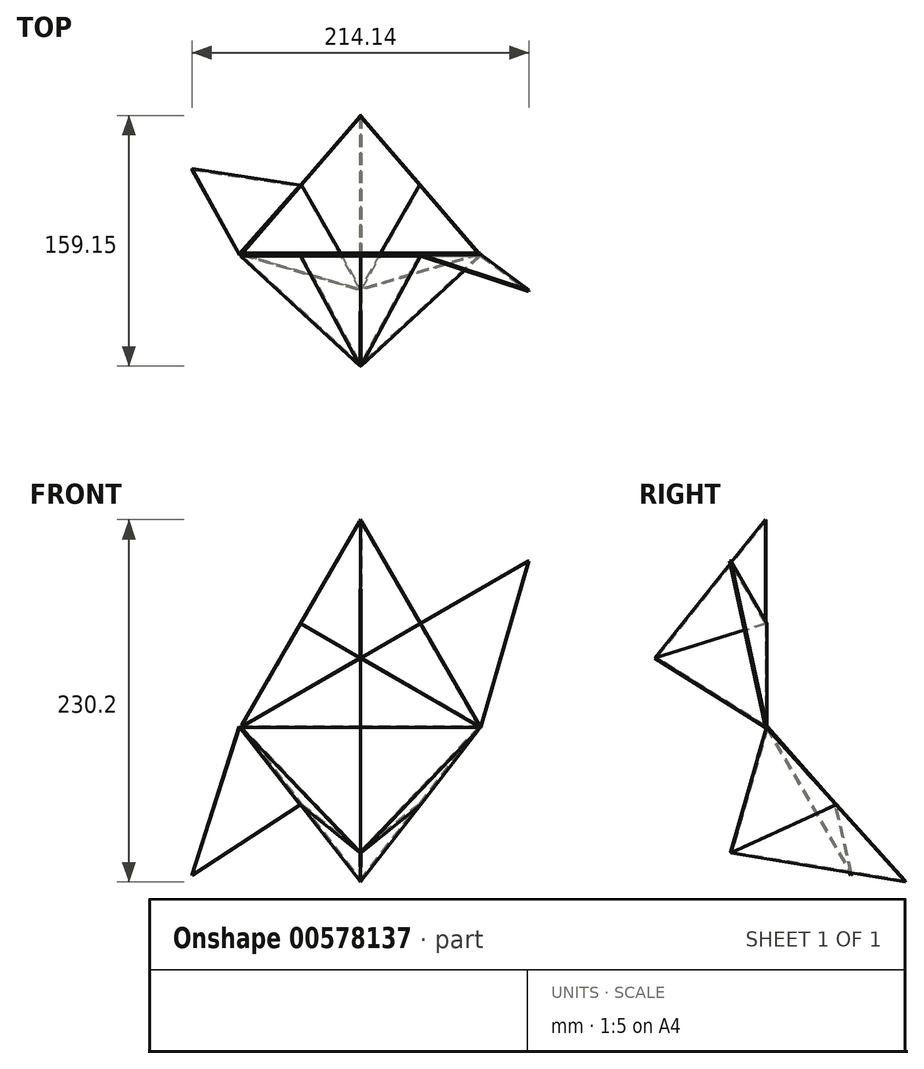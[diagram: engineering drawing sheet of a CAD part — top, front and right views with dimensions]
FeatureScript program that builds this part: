
annotation { "Feature Type Name" : "Feature", "Feature Type Description" : "" }
export const myFeature = defineFeature(function(context is Context, id is Id, definition is map)
    precondition{}
    {
        {
            var Q0;
            Q0=qCreatedBy(makeId("Front.planeOp"),FACE);
            var sketch = newSketch(context, id + "F0", { "sketchPlane" : qUnion([Q0])});
            skLineSegment(sketch, "E0", {"start": v(0, 0) * mm, "end": v(76.2, 0) * mm});
            skLineSegment(sketch, "E1", {"start": v(76.2, 0) * mm, "end": v(152.4, 0) * mm});
            skLineSegment(sketch, "E2", {"start": v(76.2, 0) * mm, "end": v(76.2, -82.55) * mm});
            skLineSegment(sketch, "E3", {"start": v(0, 0) * mm, "end": v(38.1, 66) * mm});
            skLineSegment(sketch, "E4", {"start": v(38.1, 66) * mm, "end": v(76.2, 131.98) * mm});
            skLineSegment(sketch, "E5", {"start": v(76.2, 131.98) * mm, "end": v(114.3, 66) * mm});
            skLineSegment(sketch, "E6", {"start": v(114.3, 66) * mm, "end": v(152.4, 0) * mm});
            skLineSegment(sketch, "E7", {"start": v(38.1, 66) * mm, "end": v(-33.4, 107.27) * mm});
            skLineSegment(sketch, "E8", {"start": v(114.3, 66) * mm, "end": v(185.8, 107.27) * mm});
            skLineSegment(sketch, "E9", {"start": v(0, 0) * mm, "end": v(76.2, -82.55) * mm});
            skLineSegment(sketch, "E10", {"start": v(152.4, 0) * mm, "end": v(76.2, -82.55) * mm});
            skLineSegment(sketch, "E11", {"start": v(76.2, 131.98) * mm, "end": v(185.8, 107.27) * mm});
            skLineSegment(sketch, "E12", {"start": v(152.4, 0) * mm, "end": v(185.8, 107.27) * mm});
            skLineSegment(sketch, "E13", {"start": v(76.2, 131.98) * mm, "end": v(-33.4, 107.27) * mm});
            skLineSegment(sketch, "E14", {"start": v(-33.4, 107.27) * mm, "end": v(0, 0) * mm});
            skSolve(sketch);
        }
        {
            var Q0;
            Q0=makeQuery(id+"F0.imprint","IMPRINT",FACE,{"disambiguationData":[TD([[makeQuery(id+"F0.imprint","IMPRINT",EDGE,{"derivedFrom":sQuery(id+"F0.wireOp",EDGE,"E4")}),1.0]])]});
            var Q1;
            Q1=makeQuery(id+"F0.imprint","IMPRINT",FACE,{"disambiguationData":[TD([[makeQuery(id+"F0.imprint","IMPRINT",EDGE,{"derivedFrom":sQuery(id+"F0.wireOp",EDGE,"E0")}),-1.0]])]});
            var Q2;
            Q2=makeQuery(id+"F0.imprint","IMPRINT",FACE,{"disambiguationData":[TD([[makeQuery(id+"F0.imprint","IMPRINT",EDGE,{"derivedFrom":sQuery(id+"F0.wireOp",EDGE,"E6")}),1.0]])]});
            extrude(context, id + "F1", {"entities" : qUnion([Q0, Q1, Q2]), "depth" : 1.02 * mm, "offsetDistance" : 25.4 * mm});
        }
        {
            var Q0;
            Q0=makeQuery(id+"F1.opExtrude","SWEPT_BODY",BODY,{"disambiguationData":[OSD([sQuery(id+"F0.wireOp",EDGE,"E3"),sQuery(id+"F0.wireOp",EDGE,"E4"),sQuery(id+"F0.wireOp",EDGE,"E13"),sQuery(id+"F0.wireOp",EDGE,"E14")])]});
            var Q1;
            Q1=makeQuery(id+"F1.opExtrude","CAP_EDGE",EDGE,{"disambiguationData":[OSD([sQuery(id+"F0.wireOp",EDGE,"E3"),sQuery(id+"F0.wireOp",EDGE,"E4")])],"isStart":true});
            transform(context, id + "F2", {"entities" : qUnion([Q0]), "transformType" : TransformType.ROTATION, "transformAxis" : qUnion([Q1]), "angle" : 122 * degree, "makeCopy" : false});
        }
        {
            var Q0;
            Q0=makeQuery(id+"F1.opExtrude","SWEPT_BODY",BODY,{"disambiguationData":[OSD([sQuery(id+"F0.wireOp",EDGE,"E0"),sQuery(id+"F0.wireOp",EDGE,"E1"),sQuery(id+"F0.wireOp",EDGE,"E9"),sQuery(id+"F0.wireOp",EDGE,"E10")])]});
            var Q1;
            Q1=makeQuery(id+"F1.opExtrude","CAP_EDGE",EDGE,{"disambiguationData":[OSD([sQuery(id+"F0.wireOp",EDGE,"E0"),sQuery(id+"F0.wireOp",EDGE,"E1")])],"isStart":true});
            transform(context, id + "F3", {"entities" : qUnion([Q0]), "transformType" : TransformType.ROTATION, "transformAxis" : qUnion([Q1]), "angle" : 122 * degree, "oppositeDirection" : true, "makeCopy" : false});
        }
        {
            var Q0;
            Q0=makeQuery(id+"F1.opExtrude","SWEPT_BODY",BODY,{"disambiguationData":[OSD([sQuery(id+"F0.wireOp",EDGE,"E5"),sQuery(id+"F0.wireOp",EDGE,"E6"),sQuery(id+"F0.wireOp",EDGE,"E11"),sQuery(id+"F0.wireOp",EDGE,"E12")])]});
            var Q1;
            Q1=makeQuery(id+"F1.opExtrude","CAP_EDGE",EDGE,{"disambiguationData":[OSD([sQuery(id+"F0.wireOp",EDGE,"E5"),sQuery(id+"F0.wireOp",EDGE,"E6")])],"isStart":true});
            transform(context, id + "F4", {"entities" : qUnion([Q0]), "transformType" : TransformType.ROTATION, "transformAxis" : qUnion([Q1]), "angle" : 122 * degree, "makeCopy" : false});
        }
        {
            var Q0;
            Q0=makeQuery(id+"F0.imprint","IMPRINT",FACE,{"disambiguationData":[TD([[makeQuery(id+"F0.imprint","IMPRINT",EDGE,{"derivedFrom":sQuery(id+"F0.wireOp",EDGE,"E6")}),1.0]])]});
            extrude(context, id + "F5", {"entities" : qUnion([Q0]), "oppositeDirection" : true, "depth" : 1.02 * mm, "offsetDistance" : 25.4 * mm});
        }
        {
            var Q0;
            Q0=makeQuery(id+"F1.opExtrude","SWEPT_BODY",BODY,{"disambiguationData":[OSD([sQuery(id+"F0.wireOp",EDGE,"E3"),sQuery(id+"F0.wireOp",EDGE,"E4"),sQuery(id+"F0.wireOp",EDGE,"E13"),sQuery(id+"F0.wireOp",EDGE,"E14")])]});
            var Q1;
            Q1=makeQuery(id+"F1.opExtrude","SWEPT_BODY",BODY,{"disambiguationData":[OSD([sQuery(id+"F0.wireOp",EDGE,"E5"),sQuery(id+"F0.wireOp",EDGE,"E6"),sQuery(id+"F0.wireOp",EDGE,"E11"),sQuery(id+"F0.wireOp",EDGE,"E12")])]});
            var Q2;
            Q2=makeQuery(id+"F1.opExtrude","SWEPT_BODY",BODY,{"disambiguationData":[OSD([sQuery(id+"F0.wireOp",EDGE,"E0"),sQuery(id+"F0.wireOp",EDGE,"E1"),sQuery(id+"F0.wireOp",EDGE,"E9"),sQuery(id+"F0.wireOp",EDGE,"E10")])]});
            var Q3;
            Q3=qCreatedBy(makeId("Top.planeOp"),FACE);
            mirror(context, id + "F6", {"entities" : qUnion([Q0, Q1, Q2]), "mirrorPlane" : qUnion([Q3])});
        }
        {
            var Q0;
            Q0=makeQuery(id+"F6.opPattern","COPY",BODY,{"derivedFrom":makeQuery(id+"F1.opExtrude","SWEPT_BODY",BODY,{"disambiguationData":[OSD([sQuery(id+"F0.wireOp",EDGE,"E0"),sQuery(id+"F0.wireOp",EDGE,"E1"),sQuery(id+"F0.wireOp",EDGE,"E9"),sQuery(id+"F0.wireOp",EDGE,"E10")])]}),"instanceName":"1"});
            var Q1;
            Q1=makeQuery(id+"F6.opPattern","COPY",BODY,{"derivedFrom":makeQuery(id+"F1.opExtrude","SWEPT_BODY",BODY,{"disambiguationData":[OSD([sQuery(id+"F0.wireOp",EDGE,"E5"),sQuery(id+"F0.wireOp",EDGE,"E6"),sQuery(id+"F0.wireOp",EDGE,"E11"),sQuery(id+"F0.wireOp",EDGE,"E12")])]}),"instanceName":"1"});
            var Q2;
            Q2=makeQuery(id+"F6.opPattern","COPY",BODY,{"derivedFrom":makeQuery(id+"F1.opExtrude","SWEPT_BODY",BODY,{"disambiguationData":[OSD([sQuery(id+"F0.wireOp",EDGE,"E3"),sQuery(id+"F0.wireOp",EDGE,"E4"),sQuery(id+"F0.wireOp",EDGE,"E13"),sQuery(id+"F0.wireOp",EDGE,"E14")])]}),"instanceName":"1"});
            var Q3;
            Q3=makeQuery(id+"F1.opExtrude","CAP_EDGE",EDGE,{"disambiguationData":[OSD([sQuery(id+"F0.wireOp",EDGE,"E0"),sQuery(id+"F0.wireOp",EDGE,"E1")])],"isStart":false});
            transform(context, id + "F7", {"entities" : qUnion([Q0, Q1, Q2]), "transformType" : TransformType.ROTATION, "transformAxis" : qUnion([Q3]), "angle" : 42 * degree, "makeCopy" : false});
        }
        {
            var Q0;
            Q0=sQuery(id+"F0.wireOp",VERTEX,"E3.start");
            var Q1;
            Q1=makeQuery(id+"F6.opPattern","COPY",VERTEX,{"derivedFrom":makeQuery(id+"F1.opExtrude","CAP_VERTEX",VERTEX,{"disambiguationData":[OSD([sQuery(id+"F0.wireOp",EDGE,"E4"),sQuery(id+"F0.wireOp",EDGE,"E5"),sQuery(id+"F0.wireOp",EDGE,"E11"),sQuery(id+"F0.wireOp",EDGE,"E13")]),OD(1.0)],"isStart":false}),"instanceName":"1"});
            var Q2;
            Q2=makeQuery(id+"F6.opPattern","COPY",VERTEX,{"derivedFrom":makeQuery(id+"F1.opExtrude","CAP_VERTEX",VERTEX,{"disambiguationData":[OSD([sQuery(id+"F0.wireOp",EDGE,"E7"),sQuery(id+"F0.wireOp",EDGE,"E13"),sQuery(id+"F0.wireOp",EDGE,"E14")])],"isStart":true}),"instanceName":"1"});
            cPlane(context, id + "F8", {"entities" : qUnion([Q0, Q1, Q2]), "cplaneType" : CPlaneType.THREE_POINT, "offset" : 25.4 * mm, "width" : 152.4 * mm, "height" : 152.4 * mm});
        }
        {
            var Q0;
            Q0=qCreatedBy(id+"F8.planeOp",FACE);
            var sketch = newSketch(context, id + "F9", { "sketchPlane" : qUnion([Q0])});
            skLineSegment(sketch, "E15", {"start": v(0, 0) * mm, "end": v(-21.92, -110.14) * mm});
            skLineSegment(sketch, "E16", {"start": v(-21.92, -110.14) * mm, "end": v(44.85, -61.6) * mm});
            skLineSegment(sketch, "E17", {"start": v(44.85, -61.6) * mm, "end": v(0, 0) * mm});
            skLineSegment(sketch, "E18", {"start": v(44.85, -61.6) * mm, "end": v(89.7, -123.2) * mm});
            skLineSegment(sketch, "E19", {"start": v(89.7, -123.2) * mm, "end": v(-21.92, -110.14) * mm});
            skSolve(sketch);
        }
        {
            var Q0;
            Q0=makeQuery(id+"F9.imprint","IMPRINT",FACE,{"disambiguationData":[TD([[makeQuery(id+"F9.imprint","IMPRINT",EDGE,{"derivedFrom":sQuery(id+"F9.wireOp",EDGE,"E15")}),1.0]])]});
            extrude(context, id + "F10", {"entities" : qUnion([Q0]), "oppositeDirection" : true, "depth" : 1.02 * mm, "offsetDistance" : 25.4 * mm});
        }
        {
            var Q0;
            Q0=makeQuery(id+"F10.opExtrude","SWEPT_BODY",BODY,{"disambiguationData":[OSD([sQuery(id+"F9.wireOp",EDGE,"E15"),sQuery(id+"F9.wireOp",EDGE,"E16"),sQuery(id+"F9.wireOp",EDGE,"E17")])]});
            var Q1;
            Q1=makeQuery(id+"F6.opPattern","COPY",EDGE,{"derivedFrom":makeQuery(id+"F1.opExtrude","CAP_EDGE",EDGE,{"disambiguationData":[OSD([sQuery(id+"F0.wireOp",EDGE,"E3"),sQuery(id+"F0.wireOp",EDGE,"E4")])],"isStart":true}),"instanceName":"1"});
            transform(context, id + "F11", {"entities" : qUnion([Q0]), "transformType" : TransformType.ROTATION, "transformAxis" : qUnion([Q1]), "angle" : 106 * degree, "makeCopy" : false});
        }
        {
            var Q0;
            Q0=makeQuery(id+"F5.opExtrude","SWEPT_BODY",BODY,{"disambiguationData":[OSD([sQuery(id+"F0.wireOp",EDGE,"E6"),sQuery(id+"F0.wireOp",EDGE,"E8"),sQuery(id+"F0.wireOp",EDGE,"E12")])]});
            var Q1;
            Q1=sQuery(id+"F0.wireOp",EDGE,"E6");
            transform(context, id + "F12", {"entities" : qUnion([Q0]), "transformType" : TransformType.ROTATION, "transformAxis" : qUnion([Q1]), "angle" : 16 * degree, "makeCopy" : false});
        }
        {
            var Q0;
            Q0=makeQuery(id+"F0.imprint","IMPRINT",FACE,{"disambiguationData":[TD([[makeQuery(id+"F0.imprint","IMPRINT",EDGE,{"derivedFrom":sQuery(id+"F0.wireOp",EDGE,"E3")}),1.0]])]});
            var Q1;
            Q1=makeQuery(id+"F0.imprint","IMPRINT",FACE,{"disambiguationData":[TD([[makeQuery(id+"F0.imprint","IMPRINT",EDGE,{"derivedFrom":sQuery(id+"F0.wireOp",EDGE,"E1")}),-1.0]])]});
            var Q2;
            Q2=makeQuery(id+"F0.imprint","IMPRINT",FACE,{"disambiguationData":[TD([[makeQuery(id+"F0.imprint","IMPRINT",EDGE,{"derivedFrom":sQuery(id+"F0.wireOp",EDGE,"E5")}),1.0]])]});
            extrude(context, id + "F13", {"entities" : qUnion([Q0, Q1, Q2]), "depth" : 1.02 * mm, "offsetDistance" : 25.4 * mm});
        }
        {
            var Q0;
            Q0=makeQuery(id+"F13.opExtrude","SWEPT_BODY",BODY,{"disambiguationData":[OSD([sQuery(id+"F0.wireOp",EDGE,"E3"),sQuery(id+"F0.wireOp",EDGE,"E7"),sQuery(id+"F0.wireOp",EDGE,"E14")])]});
            var Q1;
            Q1=sQuery(id+"F0.wireOp",EDGE,"E3");
            transform(context, id + "F14", {"entities" : qUnion([Q0]), "transformType" : TransformType.ROTATION, "transformAxis" : qUnion([Q1]), "angle" : 122 * degree, "makeCopy" : false});
        }
        {
            var Q0;
            Q0=makeQuery(id+"F13.opExtrude","SWEPT_BODY",BODY,{"disambiguationData":[OSD([sQuery(id+"F0.wireOp",EDGE,"E1"),sQuery(id+"F0.wireOp",EDGE,"E2"),sQuery(id+"F0.wireOp",EDGE,"E10")])]});
            var Q1;
            Q1=sQuery(id+"F0.wireOp",EDGE,"E1");
            transform(context, id + "F15", {"entities" : qUnion([Q0]), "transformType" : TransformType.ROTATION, "transformAxis" : qUnion([Q1]), "angle" : 122 * degree, "oppositeDirection" : true, "makeCopy" : false});
        }
        {
            var Q0;
            Q0=makeQuery(id+"F13.opExtrude","SWEPT_BODY",BODY,{"disambiguationData":[OSD([sQuery(id+"F0.wireOp",EDGE,"E5"),sQuery(id+"F0.wireOp",EDGE,"E8"),sQuery(id+"F0.wireOp",EDGE,"E11")])]});
            var Q1;
            Q1=sQuery(id+"F0.wireOp",EDGE,"E5");
            transform(context, id + "F16", {"entities" : qUnion([Q0]), "transformType" : TransformType.ROTATION, "transformAxis" : qUnion([Q1]), "angle" : 122 * degree, "makeCopy" : false});
        }
        {
            var Q0;
            Q0=makeQuery(id+"F13.opExtrude","SWEPT_BODY",BODY,{"disambiguationData":[OSD([sQuery(id+"F0.wireOp",EDGE,"E3"),sQuery(id+"F0.wireOp",EDGE,"E7"),sQuery(id+"F0.wireOp",EDGE,"E14")])]});
            var Q1;
            Q1=makeQuery(id+"F13.opExtrude","SWEPT_BODY",BODY,{"disambiguationData":[OSD([sQuery(id+"F0.wireOp",EDGE,"E5"),sQuery(id+"F0.wireOp",EDGE,"E8"),sQuery(id+"F0.wireOp",EDGE,"E11")])]});
            var Q2;
            Q2=makeQuery(id+"F13.opExtrude","SWEPT_BODY",BODY,{"disambiguationData":[OSD([sQuery(id+"F0.wireOp",EDGE,"E1"),sQuery(id+"F0.wireOp",EDGE,"E2"),sQuery(id+"F0.wireOp",EDGE,"E10")])]});
            var Q3;
            Q3=qCreatedBy(makeId("Top.planeOp"),FACE);
            mirror(context, id + "F17", {"entities" : qUnion([Q0, Q1, Q2]), "mirrorPlane" : qUnion([Q3])});
        }
        {
            var Q0;
            Q0=makeQuery(id+"F17.opPattern","COPY",BODY,{"derivedFrom":makeQuery(id+"F13.opExtrude","SWEPT_BODY",BODY,{"disambiguationData":[OSD([sQuery(id+"F0.wireOp",EDGE,"E1"),sQuery(id+"F0.wireOp",EDGE,"E2"),sQuery(id+"F0.wireOp",EDGE,"E10")])]}),"instanceName":"1"});
            var Q1;
            Q1=makeQuery(id+"F17.opPattern","COPY",BODY,{"derivedFrom":makeQuery(id+"F13.opExtrude","SWEPT_BODY",BODY,{"disambiguationData":[OSD([sQuery(id+"F0.wireOp",EDGE,"E5"),sQuery(id+"F0.wireOp",EDGE,"E8"),sQuery(id+"F0.wireOp",EDGE,"E11")])]}),"instanceName":"1"});
            var Q2;
            Q2=makeQuery(id+"F17.opPattern","COPY",BODY,{"derivedFrom":makeQuery(id+"F13.opExtrude","SWEPT_BODY",BODY,{"disambiguationData":[OSD([sQuery(id+"F0.wireOp",EDGE,"E3"),sQuery(id+"F0.wireOp",EDGE,"E7"),sQuery(id+"F0.wireOp",EDGE,"E14")])]}),"instanceName":"1"});
            var Q3;
            Q3=makeQuery(id+"F1.opExtrude","CAP_EDGE",EDGE,{"disambiguationData":[OSD([sQuery(id+"F0.wireOp",EDGE,"E0")])],"isStart":false});
            transform(context, id + "F18", {"entities" : qUnion([Q0, Q1, Q2]), "transformType" : TransformType.ROTATION, "transformAxis" : qUnion([Q3]), "angle" : 42 * degree, "makeCopy" : false});
        }
    });
